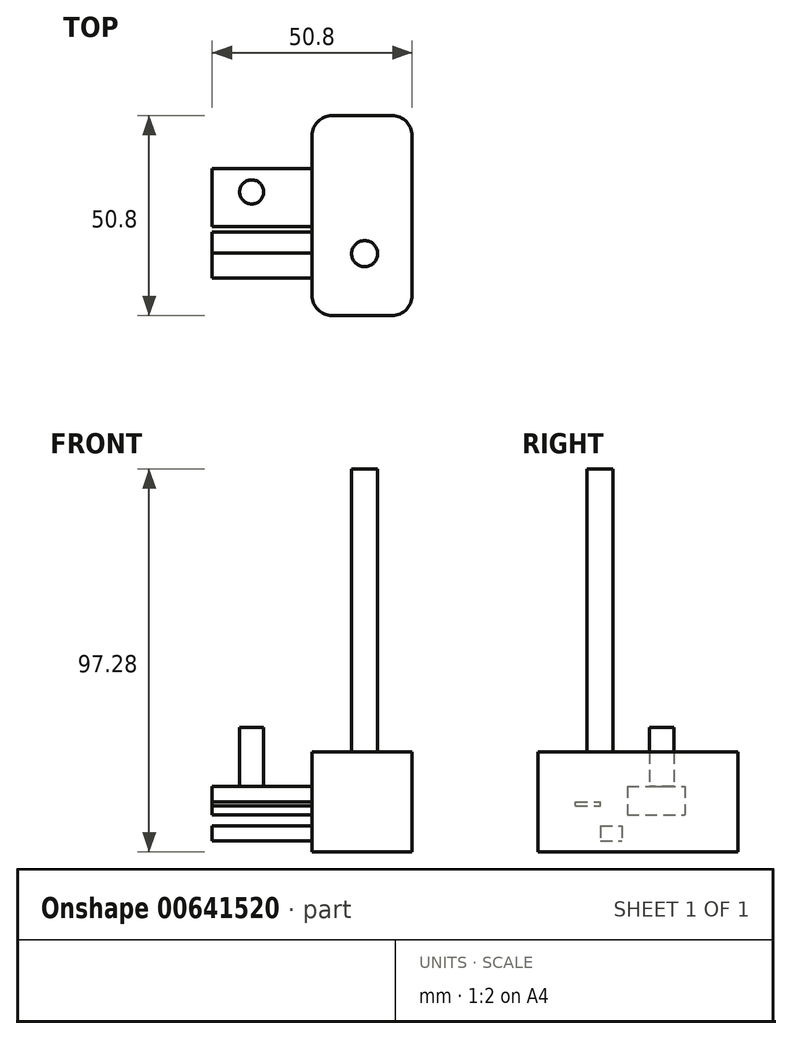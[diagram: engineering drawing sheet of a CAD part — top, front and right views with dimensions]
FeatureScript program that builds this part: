
annotation { "Feature Type Name" : "Feature", "Feature Type Description" : "" }
export const myFeature = defineFeature(function(context is Context, id is Id, definition is map)
    precondition{}
    {
        {
            var Q0;
            Q0=qCreatedBy(makeId("Top.planeOp"),FACE);
            var sketch = newSketch(context, id + "F0", { "sketchPlane" : qUnion([Q0])});
            skLineSegment(sketch, "E0.bottom", {"start": v(-25.4, 50.8) * mm, "end": v(0, 50.8) * mm});
            skLineSegment(sketch, "E0.top", {"start": v(-25.4, 0) * mm, "end": v(0, 0) * mm});
            skLineSegment(sketch, "E0.left", {"start": v(-25.4, 50.8) * mm, "end": v(-25.4, 0) * mm});
            skLineSegment(sketch, "E0.right", {"start": v(0, 50.8) * mm, "end": v(0, 0) * mm});
            skSolve(sketch);
        }
        {
            var Q0;
            Q0=makeQuery(id+"F0.imprint","IMPRINT",FACE,{"disambiguationData":[TD([[makeQuery(id+"F0.imprint","IMPRINT",EDGE,{"derivedFrom":sQuery(id+"F0.wireOp",EDGE,"E0.bottom")}),-1.0]])]});
            extrude(context, id + "F1", {"entities" : qUnion([Q0]), "depth" : 25.4 * mm, "offsetDistance" : 25.4 * mm});
        }
        {
            var Q0;
            Q0=makeQuery(id+"F1.opExtrude","SWEPT_EDGE",EDGE,{"disambiguationData":[OSD([sQuery(id+"F0.wireOp",EDGE,"E0.top"),sQuery(id+"F0.wireOp",EDGE,"E0.right")])]});
            var Q1;
            Q1=makeQuery(id+"F1.opExtrude","SWEPT_EDGE",EDGE,{"disambiguationData":[OSD([sQuery(id+"F0.wireOp",EDGE,"E0.top"),sQuery(id+"F0.wireOp",EDGE,"E0.left")])]});
            var Q2;
            Q2=makeQuery(id+"F1.opExtrude","SWEPT_EDGE",EDGE,{"disambiguationData":[OSD([sQuery(id+"F0.wireOp",EDGE,"E0.bottom"),sQuery(id+"F0.wireOp",EDGE,"E0.right")])]});
            var Q3;
            Q3=makeQuery(id+"F1.opExtrude","SWEPT_EDGE",EDGE,{"disambiguationData":[OSD([sQuery(id+"F0.wireOp",EDGE,"E0.bottom"),sQuery(id+"F0.wireOp",EDGE,"E0.left")])]});
            fillet(context, id + "F2", {"entities" : qUnion([Q0, Q1, Q2, Q3]), "radius" : 5.08 * mm, "tangentPropagation" : true, "allowEdgeOverflow" : false});
        }
        {
            var Q0;
            Q0=makeQuery(id+"F1.opExtrude","CAP_FACE",FACE,{"disambiguationData":[OSD([sQuery(id+"F0.wireOp",EDGE,"E0.bottom"),sQuery(id+"F0.wireOp",EDGE,"E0.top"),sQuery(id+"F0.wireOp",EDGE,"E0.left"),sQuery(id+"F0.wireOp",EDGE,"E0.right")])],"isStart":false});
            var sketch = newSketch(context, id + "F3", { "sketchPlane" : qUnion([Q0])});
            skCircle(sketch, "E1", {"center": v(-12.07, 15.73) * mm, "radius": 3.31 * mm});
            skSolve(sketch);
        }
        {
            var Q0;
            Q0=makeQuery(id+"F3.imprint","IMPRINT",FACE,{"disambiguationData":[TD([[makeQuery(id+"F3.imprint","IMPRINT",EDGE,{"derivedFrom":sQuery(id+"F3.wireOp",EDGE,"E1")}),1.0]])]});
            extrude(context, id + "F4", {"entities" : qUnion([Q0]), "operationType" : NewBodyOperationType.ADD, "depth" : 71.88 * mm, "offsetDistance" : 25.4 * mm});
        }
        {
            var Q0;
            Q0=makeQuery(id+"F1.opExtrude","SWEPT_FACE",FACE,{"disambiguationData":[OSD([sQuery(id+"F0.wireOp",EDGE,"E0.left")])]});
            var sketch = newSketch(context, id + "F5", { "sketchPlane" : qUnion([Q0])});
            skLineSegment(sketch, "E2.bottom", {"start": v(-9.54, 11.67) * mm, "end": v(-15.84, 11.67) * mm});
            skLineSegment(sketch, "E2.top", {"start": v(-9.54, 12.65) * mm, "end": v(-15.84, 12.65) * mm});
            skLineSegment(sketch, "E2.left", {"start": v(-9.54, 11.67) * mm, "end": v(-9.54, 12.65) * mm});
            skLineSegment(sketch, "E2.right", {"start": v(-15.84, 11.67) * mm, "end": v(-15.84, 12.65) * mm});
            skLineSegment(sketch, "E3.bottom", {"start": v(-22.65, 16.67) * mm, "end": v(-37.34, 16.67) * mm});
            skLineSegment(sketch, "E3.top", {"start": v(-22.65, 9.36) * mm, "end": v(-37.34, 9.36) * mm});
            skLineSegment(sketch, "E3.left", {"start": v(-22.65, 16.67) * mm, "end": v(-22.65, 9.36) * mm});
            skLineSegment(sketch, "E3.right", {"start": v(-37.34, 16.67) * mm, "end": v(-37.34, 9.36) * mm});
            skLineSegment(sketch, "E4.bottom", {"start": v(-15.84, 6.56) * mm, "end": v(-21.26, 6.56) * mm});
            skLineSegment(sketch, "E4.top", {"start": v(-15.84, 2.77) * mm, "end": v(-21.26, 2.77) * mm});
            skLineSegment(sketch, "E4.left", {"start": v(-15.84, 6.56) * mm, "end": v(-15.84, 2.77) * mm});
            skLineSegment(sketch, "E4.right", {"start": v(-21.26, 6.56) * mm, "end": v(-21.26, 2.77) * mm});
            skSolve(sketch);
        }
        {
            var Q0;
            Q0=makeQuery(id+"F5.imprint","IMPRINT",FACE,{"disambiguationData":[TD([[makeQuery(id+"F5.imprint","IMPRINT",EDGE,{"derivedFrom":sQuery(id+"F5.wireOp",EDGE,"E2.bottom")}),-1.0]])]});
            var Q1;
            Q1=makeQuery(id+"F5.imprint","IMPRINT",FACE,{"disambiguationData":[TD([[makeQuery(id+"F5.imprint","IMPRINT",EDGE,{"derivedFrom":sQuery(id+"F5.wireOp",EDGE,"E4.bottom")}),1.0]])]});
            var Q2;
            Q2=makeQuery(id+"F5.imprint","IMPRINT",FACE,{"disambiguationData":[TD([[makeQuery(id+"F5.imprint","IMPRINT",EDGE,{"derivedFrom":sQuery(id+"F5.wireOp",EDGE,"E3.bottom")}),1.0]])]});
            extrude(context, id + "F6", {"entities" : qUnion([Q0, Q1, Q2]), "operationType" : NewBodyOperationType.ADD, "depth" : 25.4 * mm, "offsetDistance" : 25.4 * mm});
        }
        {
            var Q0;
            Q0=makeQuery(id+"F6.opExtrude","SWEPT_FACE",FACE,{"disambiguationData":[OSD([sQuery(id+"F5.wireOp",EDGE,"E3.bottom")])]});
            var sketch = newSketch(context, id + "F7", { "sketchPlane" : qUnion([Q0])});
            skCircle(sketch, "E5", {"center": v(-40.76, 31.4) * mm, "radius": 3.06 * mm});
            skSolve(sketch);
        }
        {
            var Q0;
            Q0=makeQuery(id+"F7.imprint","IMPRINT",FACE,{"disambiguationData":[TD([[makeQuery(id+"F7.imprint","IMPRINT",EDGE,{"derivedFrom":sQuery(id+"F7.wireOp",EDGE,"E5")}),1.0]])]});
            extrude(context, id + "F8", {"entities" : qUnion([Q0]), "operationType" : NewBodyOperationType.ADD, "depth" : 15 * mm, "offsetDistance" : 25.4 * mm});
        }
    });
